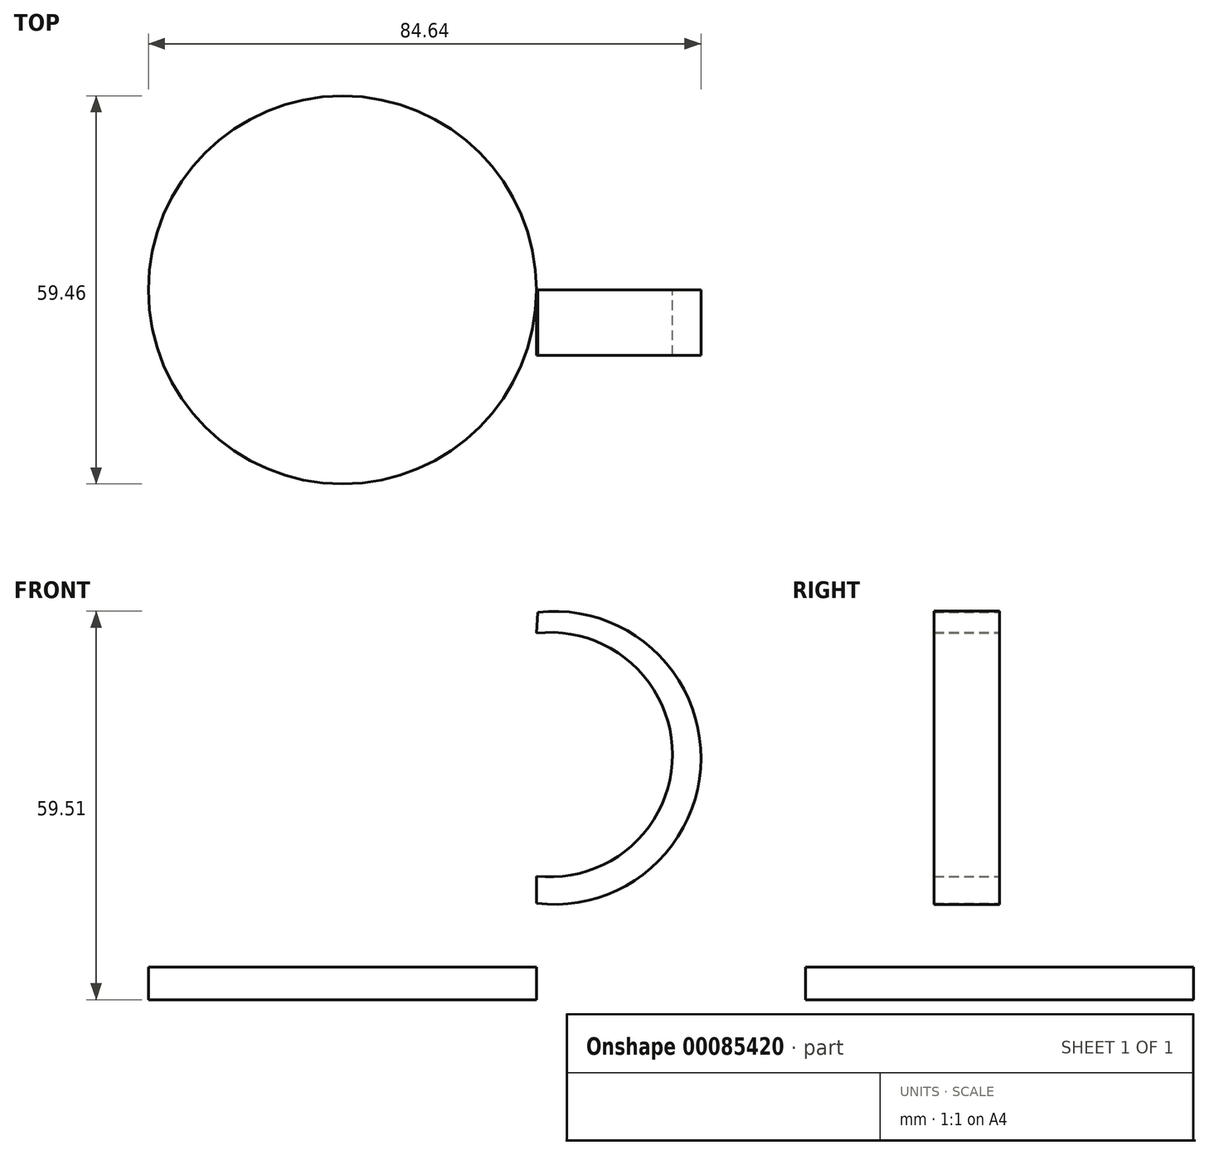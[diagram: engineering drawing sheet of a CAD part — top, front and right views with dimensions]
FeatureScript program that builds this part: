
annotation { "Feature Type Name" : "Feature", "Feature Type Description" : "" }
export const myFeature = defineFeature(function(context is Context, id is Id, definition is map)
    precondition{}
    {
        {
            var Q0;
            Q0=qCreatedBy(makeId("Top.planeOp"),FACE);
            var sketch = newSketch(context, id + "F0", { "sketchPlane" : qUnion([Q0])});
            skCircle(sketch, "E0", {"center": v(0, 0) * mm, "radius": 30 * mm});
            skSolve(sketch);
        }
        {
            var Q0;
            Q0=sQuery(id+"F0.wireOp",EDGE,"E0");
            extrude(context, id + "F1", {"bodyType" : ToolBodyType.SURFACE, "surfaceEntities" : qUnion([Q0]), "depth" : 80 * mm});
        }
        {
            var Q0;
            Q0=qCreatedBy(makeId("Front.planeOp"),FACE);
            var sketch = newSketch(context, id + "F2", { "sketchPlane" : qUnion([Q0])});
            skArc(sketch, "E1", {"start": v(29.75, 14.75) * mm, "mid": v(54.91, 36.95) * mm, "end": v(29.94, 59.37) * mm});
            skArc(sketch, "E2", {"start": v(29.75, 18.92) * mm, "mid": v(50.56, 37.54) * mm, "end": v(29.75, 56.16) * mm});
            skLineSegment(sketch, "E3", {"start": v(29.75, 14.75) * mm, "end": v(29.75, 18.92) * mm});
            skLineSegment(sketch, "E4", {"start": v(29.75, 56.16) * mm, "end": v(29.94, 59.37) * mm});
            skSolve(sketch);
        }
        {
            var Q0;
            Q0 = qSketchRegion(id + "F2", true);
            extrude(context, id + "F3", {"entities" : qUnion([Q0]), "depth" : 10 * mm});
        }
        {
            var Q0;
            Q0=qCreatedBy(makeId("Top.planeOp"),FACE);
            var sketch = newSketch(context, id + "F4", { "sketchPlane" : qUnion([Q0])});
            skCircle(sketch, "E5", {"center": v(0, 0) * mm, "radius": 29.73 * mm});
            skSolve(sketch);
        }
        {
            var Q0;
            Q0 = qSketchRegion(id + "F4", true);
            extrude(context, id + "F5", {"entities" : qUnion([Q0]), "depth" : 5 * mm});
        }
    });
